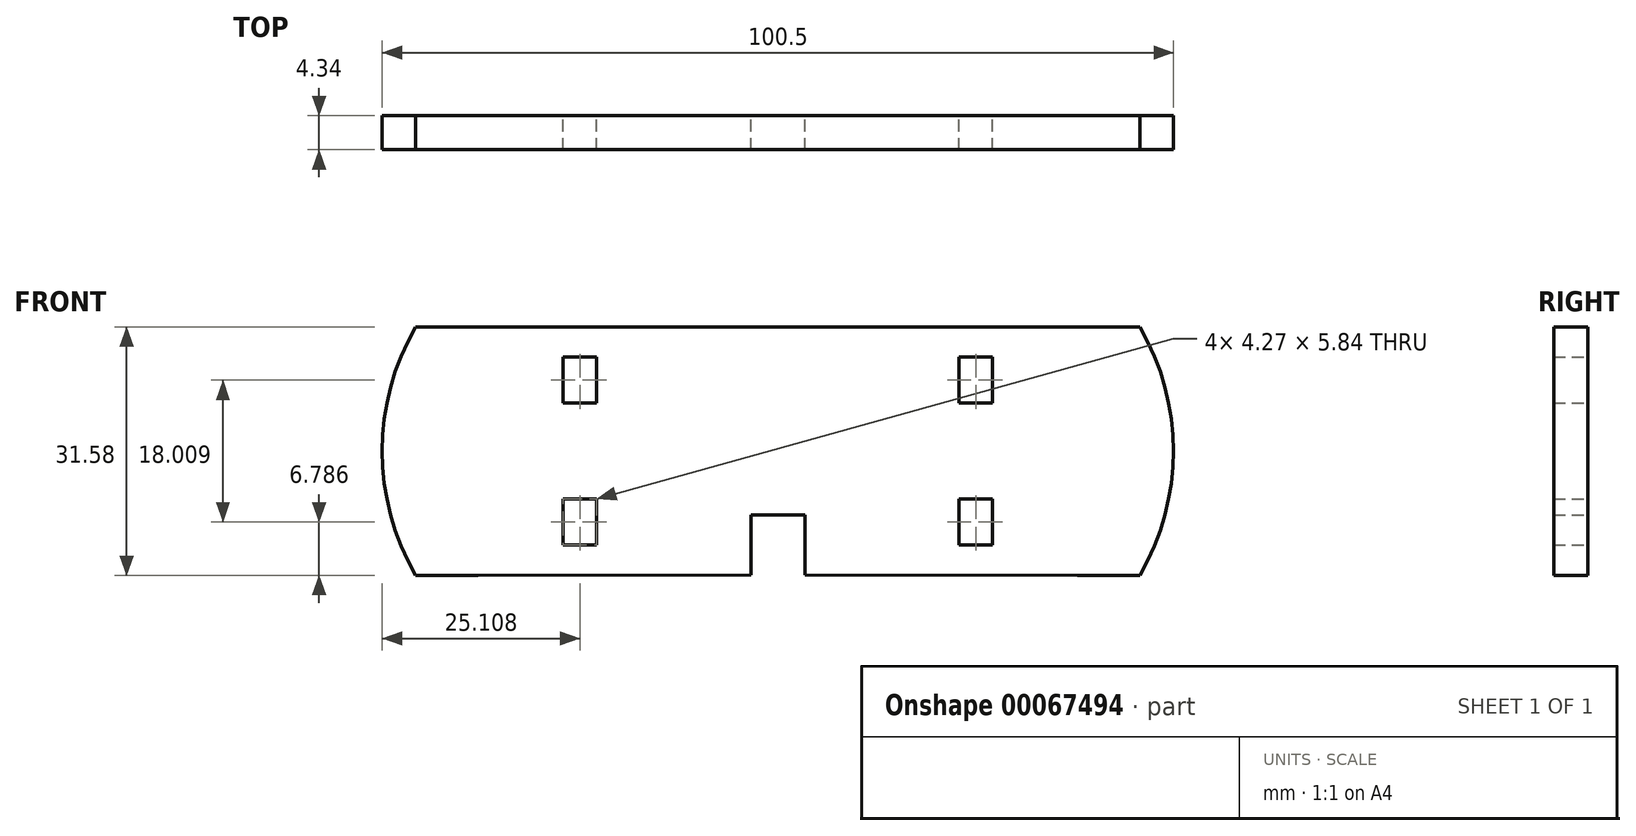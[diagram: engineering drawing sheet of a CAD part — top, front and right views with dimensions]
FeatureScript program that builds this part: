
annotation { "Feature Type Name" : "Feature", "Feature Type Description" : "" }
export const myFeature = defineFeature(function(context is Context, id is Id, definition is map)
    precondition{}
    {
        {
            var Q0;
            Q0=qCreatedBy(makeId("Front.planeOp"),FACE);
            var sketch = newSketch(context, id + "F0", { "sketchPlane" : qUnion([Q0])});
            skLineSegment(sketch, "E0.top", {"start": v(38.08, 15.79) * mm, "end": v(-38.08, 15.79) * mm});
            skLineSegment(sketch, "E0.left", {"start": v(38.08, -15.79) * mm, "end": v(38.08, 15.79) * mm});
            skLineSegment(sketch, "E0.right", {"start": v(-38.08, -15.79) * mm, "end": v(-38.08, 15.79) * mm});
            skPoint(sketch, "E0.middle", {"position": v(0, 0) * mm});
            skLineSegment(sketch, "E1", {"start": v(-38.08, 9) * mm, "end": v(-25.15, 9) * mm, "construction": true});
            skLineSegment(sketch, "E2", {"start": v(-25.15, 15.79) * mm, "end": v(-25.15, 9) * mm, "construction": true});
            skLineSegment(sketch, "E3.bottom", {"start": v(-23.02, 6.08) * mm, "end": v(-27.29, 6.08) * mm});
            skLineSegment(sketch, "E3.top", {"start": v(-23.02, 11.93) * mm, "end": v(-27.29, 11.93) * mm});
            skLineSegment(sketch, "E3.left", {"start": v(-23.02, 6.08) * mm, "end": v(-23.02, 11.93) * mm});
            skLineSegment(sketch, "E3.right", {"start": v(-27.29, 6.08) * mm, "end": v(-27.29, 11.93) * mm});
            skPoint(sketch, "E3.middle", {"position": v(-25.15, 9) * mm});
            skLineSegment(sketch, "E4", {"start": v(-38.08, 0) * mm, "end": v(38.08, 0) * mm, "construction": true});
            skLineSegment(sketch, "E5", {"start": v(0, 15.79) * mm, "end": v(0, -15.79) * mm, "construction": true});
            skLineSegment(sketch, "E6.MirrorCS", {"start": v(23.02, 6.08) * mm, "end": v(27.29, 6.08) * mm});
            skLineSegment(sketch, "E7.MirrorCS", {"start": v(23.02, 6.08) * mm, "end": v(23.02, 11.93) * mm});
            skLineSegment(sketch, "E8.MirrorCS", {"start": v(23.02, 11.93) * mm, "end": v(27.29, 11.93) * mm});
            skLineSegment(sketch, "E9.MirrorCS", {"start": v(27.29, 6.08) * mm, "end": v(27.29, 11.93) * mm});
            skLineSegment(sketch, "E10.MirrorCS", {"start": v(-23.02, -6.08) * mm, "end": v(-23.02, -11.93) * mm});
            skLineSegment(sketch, "E11.MirrorCS", {"start": v(-23.02, -11.93) * mm, "end": v(-27.29, -11.93) * mm});
            skLineSegment(sketch, "E12.MirrorCS", {"start": v(-23.02, -6.08) * mm, "end": v(-27.29, -6.08) * mm});
            skLineSegment(sketch, "E13.MirrorCS", {"start": v(-27.29, -6.08) * mm, "end": v(-27.29, -11.93) * mm});
            skLineSegment(sketch, "E14.MirrorCS", {"start": v(23.02, -6.08) * mm, "end": v(27.29, -6.08) * mm});
            skLineSegment(sketch, "E15.MirrorCS", {"start": v(27.29, -6.08) * mm, "end": v(27.29, -11.93) * mm});
            skLineSegment(sketch, "E16.MirrorCS", {"start": v(23.02, -11.93) * mm, "end": v(27.29, -11.93) * mm});
            skLineSegment(sketch, "E17.MirrorCS", {"start": v(23.02, -6.08) * mm, "end": v(23.02, -11.93) * mm});
            skLineSegment(sketch, "E18", {"start": v(-38.08, -15.79) * mm, "end": v(-46, -15.79) * mm});
            skLineSegment(sketch, "E19", {"start": v(-46, 15.79) * mm, "end": v(-38.08, 15.79) * mm});
            skLineSegment(sketch, "E20", {"start": v(38.08, -15.79) * mm, "end": v(45.97, -15.79) * mm});
            skPoint(sketch, "E20.endSnap0", {"position": v(53.87, 0) * mm});
            skLineSegment(sketch, "E21", {"start": v(45.97, 15.79) * mm, "end": v(38.08, 15.79) * mm});
            skLineSegment(sketch, "E22", {"start": v(-46, 15.79) * mm, "end": v(-46, -15.79) * mm});
            skLineSegment(sketch, "E23", {"start": v(45.97, 15.79) * mm, "end": v(45.97, -15.79) * mm});
            skPoint(sketch, "E24.orphan", {"position": v(-53.9, 15.79) * mm});
            skPoint(sketch, "E25.orphan", {"position": v(-53.9, -15.79) * mm});
            skPoint(sketch, "E26.orphan", {"position": v(53.87, -15.79) * mm});
            skPoint(sketch, "E27.orphan", {"position": v(53.87, 15.79) * mm});
            skArc(sketch, "E28", {"start": v(-46, 15.79) * mm, "mid": v(-50.26, 0) * mm, "end": v(-46, -15.79) * mm});
            skArc(sketch, "E29", {"start": v(45.97, -15.79) * mm, "mid": v(50.24, 0) * mm, "end": v(45.97, 15.79) * mm});
            skLineSegment(sketch, "E30.bottom", {"start": v(-3.44, -8.14) * mm, "end": v(3.41, -8.14) * mm});
            skLineSegment(sketch, "E30.top", {"start": v(-0.01, -15.76) * mm, "end": v(0, -15.76) * mm});
            skLineSegment(sketch, "E30.left", {"start": v(-3.44, -8.14) * mm, "end": v(-3.44, -15.76) * mm});
            skLineSegment(sketch, "E30.right", {"start": v(3.41, -8.14) * mm, "end": v(3.41, -15.76) * mm});
            skPoint(sketch, "E31", {"position": v(-0.01, -15.76) * mm});
            skLineSegment(sketch, "E32", {"start": v(-38.08, -15.79) * mm, "end": v(-3.44, -15.76) * mm});
            skLineSegment(sketch, "E33", {"start": v(3.41, -15.76) * mm, "end": v(38.08, -15.79) * mm});
            skSolve(sketch);
        }
        {
            var Q0;
            Q0 = qSketchRegion(id + "F0", true);
            extrude(context, id + "F1", {"entities" : qUnion([Q0]), "depth" : 4.34 * mm});
        }
    });
